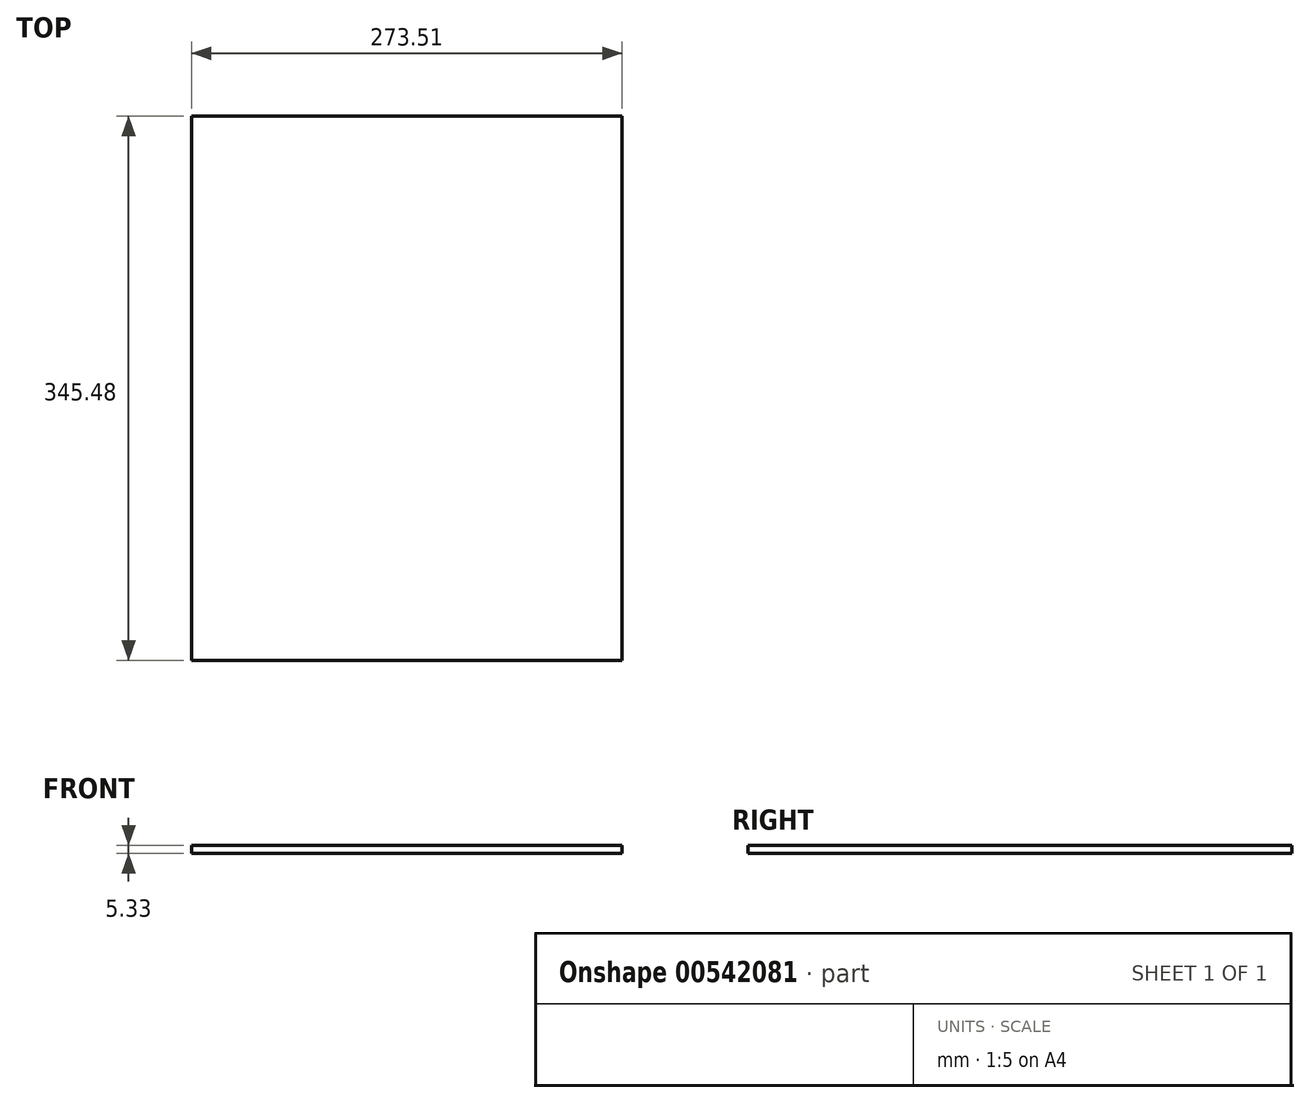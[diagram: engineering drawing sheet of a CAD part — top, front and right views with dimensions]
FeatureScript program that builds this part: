
annotation { "Feature Type Name" : "Feature", "Feature Type Description" : "" }
export const myFeature = defineFeature(function(context is Context, id is Id, definition is map)
    precondition{}
    {
        {
            var Q0;
            Q0=qCreatedBy(makeId("Top.planeOp"),FACE);
            var sketch = newSketch(context, id + "F0", { "sketchPlane" : qUnion([Q0])});
            skLineSegment(sketch, "E0.bottom", {"start": v(-157.58, 127.02) * mm, "end": v(115.93, 127.02) * mm});
            skLineSegment(sketch, "E0.top", {"start": v(-157.58, -218.46) * mm, "end": v(115.93, -218.46) * mm});
            skLineSegment(sketch, "E0.left", {"start": v(-157.58, 127.02) * mm, "end": v(-157.58, -218.46) * mm});
            skLineSegment(sketch, "E0.right", {"start": v(115.93, 127.02) * mm, "end": v(115.93, -218.46) * mm});
            skSolve(sketch);
        }
        {
            var Q0;
            Q0 = qSketchRegion(id + "F0", true);
            extrude(context, id + "F1", {"entities" : qUnion([Q0]), "depth" : 5.33 * mm, "offsetDistance" : 25.4 * mm});
        }
    });
